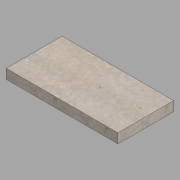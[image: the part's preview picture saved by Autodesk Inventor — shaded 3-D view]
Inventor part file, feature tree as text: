
AUTODESK INVENTOR PART (.ipt)
format: ipt  version: 2022 (Build 260153000, 153)  size: 115,200 bytes
history: native  units: in
note: dims shown in document units (in); Inventor stores cm internally (conversion verified against a paired STEP export)
features: other x1, extrude x1, sketch x1
ambient origin geometry x8: Origin, YZ Plane, XZ Plane, XY Plane, X Axis, Y Axis, Z Axis, Center Point
bodies: Body1 (feature_tree)
feature tree (3):
  other  "Type 1 paver vehicular"
  extrude  "Extrusion1"  Depth=24.0in
  sketch  "Sketch2"  dims[d0=48.0in d1=24.0in d2=4.125in d3=0.0in]
